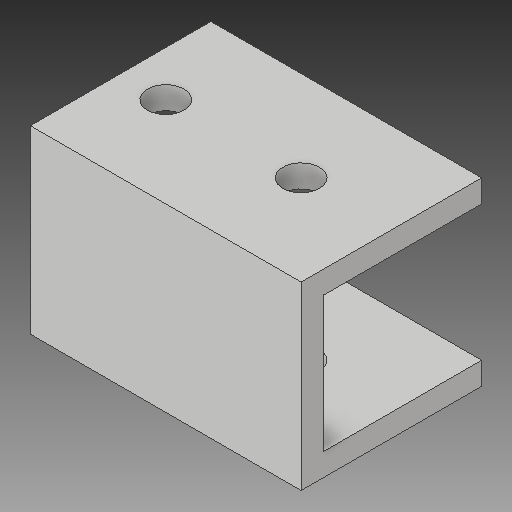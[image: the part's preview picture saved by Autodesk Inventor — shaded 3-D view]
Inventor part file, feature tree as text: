
AUTODESK INVENTOR PART (.ipt)
format: ipt  version: 2018 (Build 220112000, 112)  size: 114,688 bytes
history: native  units: in
note: dims shown in document units (in); Inventor stores cm internally (conversion verified against a paired STEP export)
features: sketch x4, other x3
ambient origin geometry x8: Origin, YZ Plane, XZ Plane, XY Plane, X Axis, Y Axis, Z Axis, Center Point
bodies: Solid1 (feature_tree)
feature tree (7):
  other  "wheel tip connector 1_MIR.ipt"
  other  "Solid1::wheel tip connector 1_MIR.ipt"
  other  "TaggingFeature1"
  sketch  "Sketch1"  dims[d0=0.3937in]
  sketch  "Sketch2"
  sketch  "Sketch3"
  sketch  "Sketch4"
